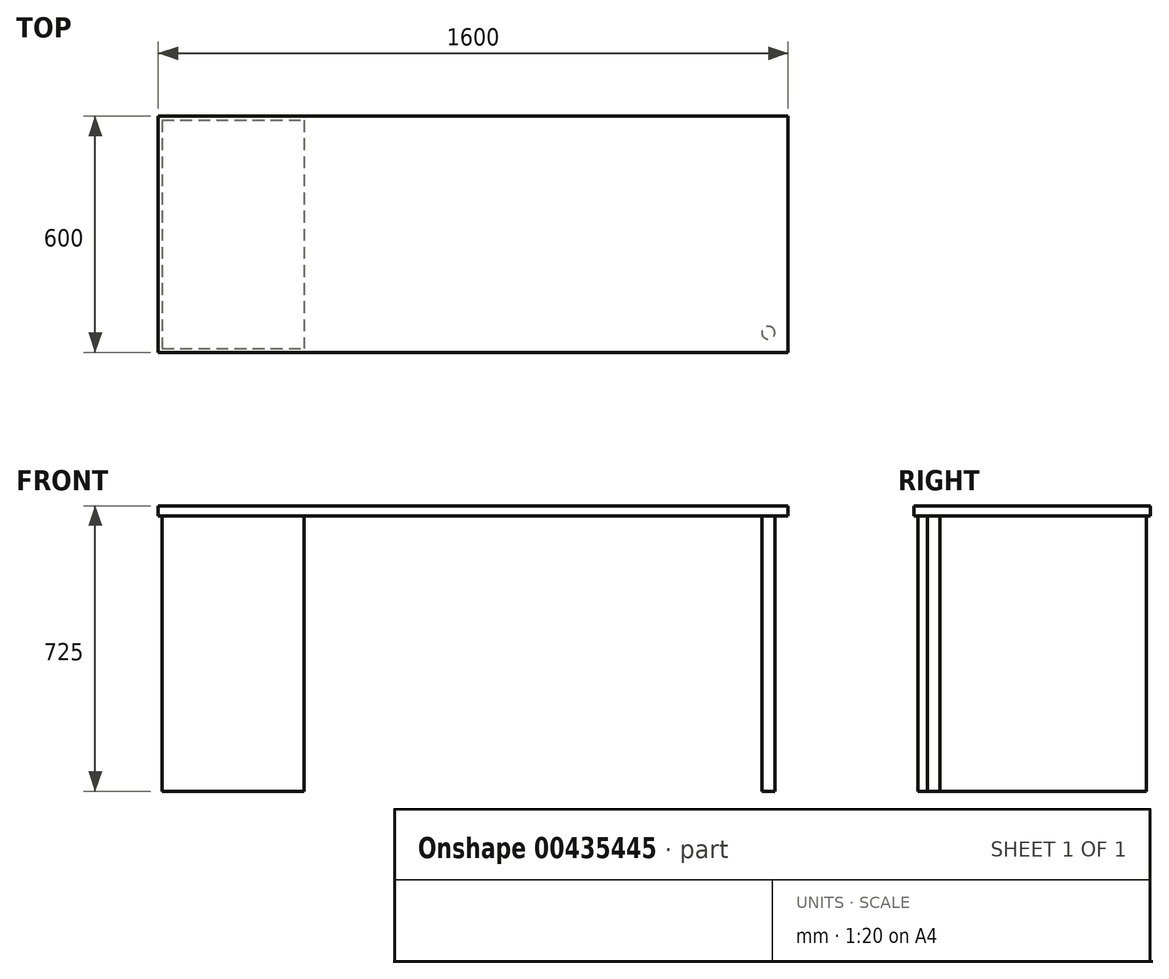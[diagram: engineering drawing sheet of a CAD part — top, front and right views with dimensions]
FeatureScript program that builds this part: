
annotation { "Feature Type Name" : "Feature", "Feature Type Description" : "" }
export const myFeature = defineFeature(function(context is Context, id is Id, definition is map)
    precondition{}
    {
        {
            var Q0;
            Q0=qCreatedBy(makeId("Top.planeOp"),FACE);
            var sketch = newSketch(context, id + "F0", { "sketchPlane" : qUnion([Q0])});
            skLineSegment(sketch, "E0.bottom", {"start": v(-800, 300) * mm, "end": v(800, 300) * mm});
            skLineSegment(sketch, "E0.top", {"start": v(-800, -300) * mm, "end": v(800, -300) * mm});
            skLineSegment(sketch, "E0.left", {"start": v(-800, 300) * mm, "end": v(-800, -300) * mm});
            skLineSegment(sketch, "E0.right", {"start": v(800, 300) * mm, "end": v(800, -300) * mm});
            skLineSegment(sketch, "E1", {"start": v(-800, 0) * mm, "end": v(800, 0) * mm, "construction": true});
            skLineSegment(sketch, "E2", {"start": v(0, -300) * mm, "end": v(0, 300) * mm, "construction": true});
            skSolve(sketch);
        }
        {
            var Q0;
            Q0=makeQuery(id+"F0.imprint","IMPRINT",FACE,{"disambiguationData":[TD([[makeQuery(id+"F0.imprint","IMPRINT",EDGE,{"derivedFrom":sQuery(id+"F0.wireOp",EDGE,"E0.bottom")}),-1.0]])]});
            extrude(context, id + "F1", {"entities" : qUnion([Q0]), "depth" : 725 * mm, "hasSecondDirection" : true, "secondDirectionOppositeDirection" : false, "secondDirectionDepth" : 700 * mm});
        }
        {
            var Q0;
            Q0=qCreatedBy(makeId("Top.planeOp"),FACE);
            var sketch = newSketch(context, id + "F2", { "sketchPlane" : qUnion([Q0])});
            skLineSegment(sketch, "E3.bottom", {"start": v(-790, 290) * mm, "end": v(-430, 290) * mm});
            skLineSegment(sketch, "E3.top", {"start": v(-790, -290) * mm, "end": v(-430, -290) * mm});
            skLineSegment(sketch, "E3.left", {"start": v(-790, 290) * mm, "end": v(-790, -290) * mm});
            skLineSegment(sketch, "E3.right", {"start": v(-430, 290) * mm, "end": v(-430, -290) * mm});
            skLineSegment(sketch, "E4", {"start": v(-790, 0) * mm, "end": v(-430, 0) * mm, "construction": true});
            skSolve(sketch);
        }
        {
            var Q0;
            Q0=makeQuery(id+"F2.imprint","IMPRINT",FACE,{"disambiguationData":[TD([[makeQuery(id+"F2.imprint","IMPRINT",EDGE,{"derivedFrom":sQuery(id+"F2.wireOp",EDGE,"E3.bottom")}),-1.0]])]});
            extrude(context, id + "F3", {"entities" : qUnion([Q0]), "depth" : 700 * mm});
        }
        {
            var Q0;
            Q0=qCreatedBy(makeId("Top.planeOp"),FACE);
            var sketch = newSketch(context, id + "F4", { "sketchPlane" : qUnion([Q0])});
            skCircle(sketch, "E5", {"center": v(750, -250) * mm, "radius": 16.35 * mm});
            skSolve(sketch);
        }
        {
            var Q0;
            Q0=makeQuery(id+"F4.imprint","IMPRINT",FACE,{"disambiguationData":[TD([[makeQuery(id+"F4.imprint","IMPRINT",EDGE,{"derivedFrom":sQuery(id+"F4.wireOp",EDGE,"E5")}),1.0]])]});
            var Q1;
            Q1=makeQuery(id+"F4.imprint","IMPRINT",FACE,{"disambiguationData":[TD([[makeQuery(id+"F4.imprint","IMPRINT",EDGE,{"derivedFrom":sQuery(id+"F4.wireOp",EDGE,"UEWGn4gV-35Ty-Ci0G-6Hpi-s7Gy5H98C1Kz")}),1.0]])]});
            extrude(context, id + "F5", {"entities" : qUnion([Q0, Q1]), "depth" : 700 * mm});
        }
    });
